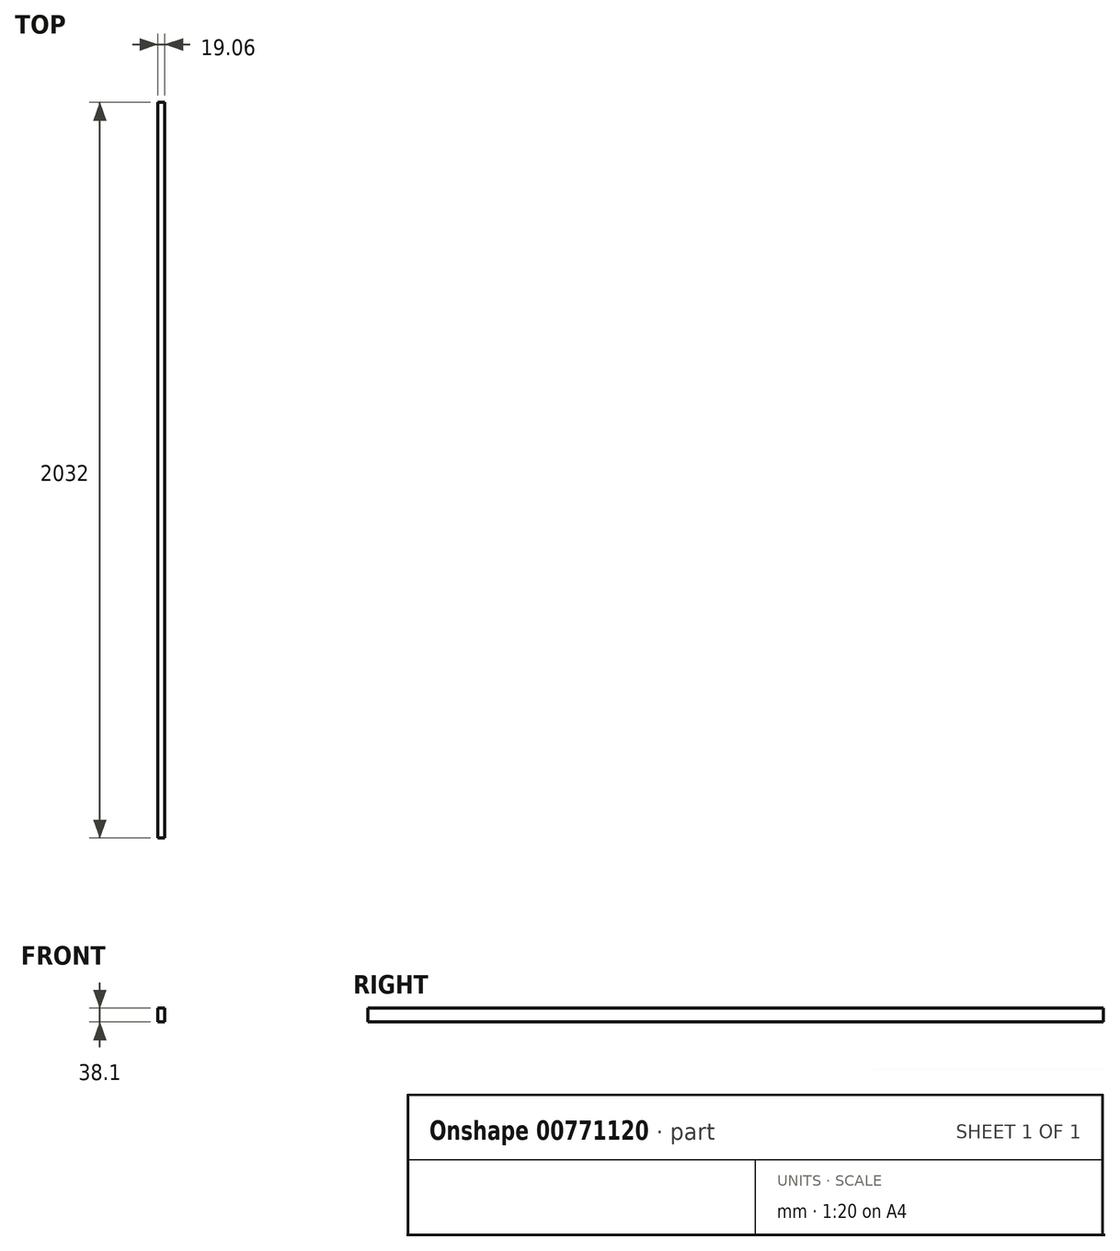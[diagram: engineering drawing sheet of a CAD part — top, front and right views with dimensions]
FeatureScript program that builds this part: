
annotation { "Feature Type Name" : "Feature", "Feature Type Description" : "" }
export const myFeature = defineFeature(function(context is Context, id is Id, definition is map)
    precondition{}
    {
        {
            var Q0;
            Q0=qCreatedBy(makeId("Front.planeOp"),FACE);
            var sketch = newSketch(context, id + "F0", { "sketchPlane" : qUnion([Q0])});
            skLineSegment(sketch, "E0.bottom", {"start": v(9.52, 19.05) * mm, "end": v(-9.53, 19.05) * mm});
            skLineSegment(sketch, "E0.top", {"start": v(9.53, -19.05) * mm, "end": v(-9.53, -19.05) * mm});
            skLineSegment(sketch, "E0.left", {"start": v(9.52, 19.05) * mm, "end": v(9.53, -19.05) * mm});
            skLineSegment(sketch, "E0.right", {"start": v(-9.53, 19.05) * mm, "end": v(-9.53, -19.05) * mm});
            skPoint(sketch, "E0.middle", {"position": v(0, 0) * mm});
            skSolve(sketch);
        }
        {
            var Q0;
            Q0=makeQuery(id+"F0.imprint","IMPRINT",FACE,{"disambiguationData":[TD([[makeQuery(id+"F0.imprint","IMPRINT",EDGE,{"derivedFrom":sQuery(id+"F0.wireOp",EDGE,"E0.bottom")}),1.0]])]});
            extrude(context, id + "F1", {"entities" : qUnion([Q0]), "endBound" : BoundingType.SYMMETRIC, "depth" : 2032 * mm, "offsetDistance" : 25.4 * mm});
        }
    });
